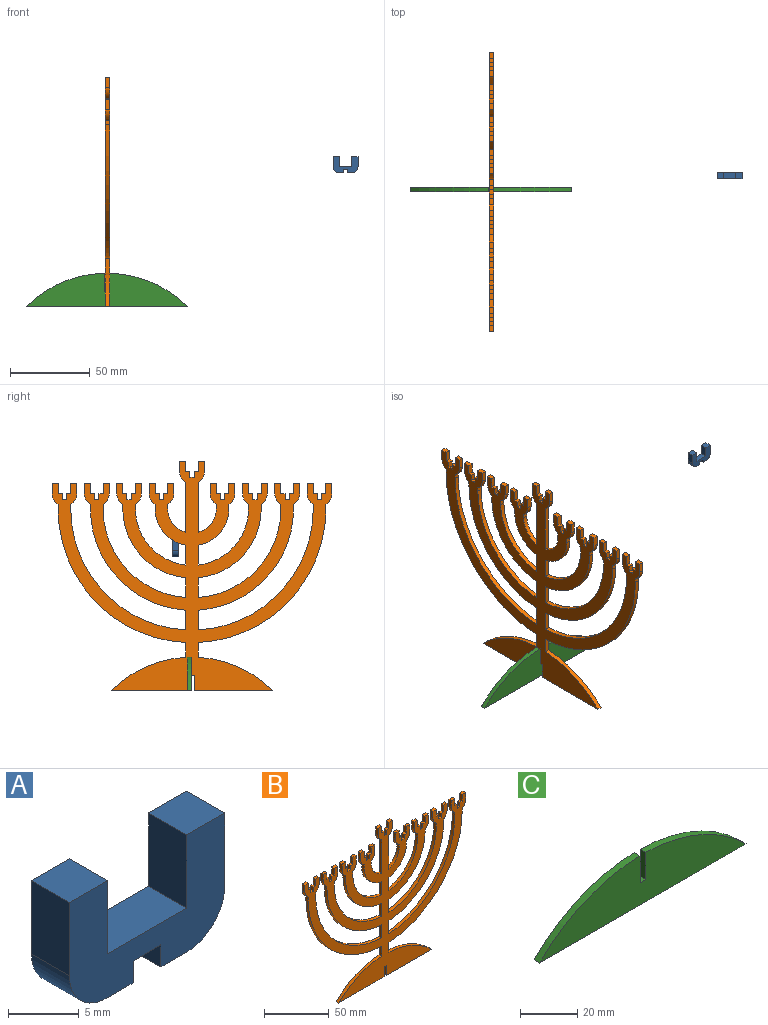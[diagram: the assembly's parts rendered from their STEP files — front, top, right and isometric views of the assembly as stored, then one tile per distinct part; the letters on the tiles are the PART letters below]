
ASSEMBLY  parts=3 mates=3
PART A: 16 faces, bbox 15.6x3.8x10.2 mm
  f0: cylinder r=3.81mm len=3.81mm, axis (0,1,0), area 22.8mm2, adj f1,f13,f14,f15
  f1: plane 6.35x3.81mm, normal (1,0,0), area 24.2mm2, adj f0,f2,f14,f15
  f2: plane 3.81x3.81mm, normal (0,0,1), area 14.5mm2, adj f1,f3,f14,f15
  f3: plane 6.35x3.81mm, normal (-1,0,0), area 24.2mm2, adj f2,f4,f14,f15
  f4: plane 7.94x3.81mm, normal (0,0,1), area 30.2mm2, adj f3,f5,f14,f15
  f5: plane 6.35x3.81mm, normal (1,0,0), area 24.2mm2, adj f4,f6,f14,f15
  f6: plane 3.81x3.81mm, normal (0,0,1), area 14.5mm2, adj f5,f7,f14,f15
  f7: plane 6.35x3.81mm, normal (-1,0,0), area 24.2mm2, adj f6,f8,f14,f15
  f8: cylinder r=3.81mm len=3.81mm, axis (0,1,0), area 22.8mm2, adj f7,f9,f14,f15
  f9: plane 3.81x2.57mm, normal (0,0,-1), area 9.8mm2, adj f8,f10,f14,f15
  f10: plane 3.81x1.91mm, normal (1,0,0), area 7.3mm2, adj f9,f11,f14,f15
  f11: plane 3.81x2.79mm, normal (0,0,-1), area 10.6mm2, adj f10,f12,f14,f15
  f12: plane 3.81x1.91mm, normal (-1,0,0), area 7.3mm2, adj f11,f13,f14,f15
  f13: plane 3.81x2.57mm, normal (0,0,-1), area 9.8mm2, adj f0,f12,f14,f15
  f14: plane 15.56x10.16mm, normal (0,-1,0), area 96.1mm2, adj f0,f1,f2,f3,f4,f5,f6,f7
  f15: plane 15.56x10.16mm, normal (0,1,0), area 96.1mm2, adj f0,f1,f2,f3,f4,f5,f6,f7
PART B: 168 faces, bbox 175.9x2.8x144.1 mm
  f0: plane 49.4x2.79mm, normal (0,0,-1), area 138mm2, adj f1,f2,f7,f167
  f1: plane 175.9x144.15mm, normal (0,-1,0), area 8346.4mm2, adj f0,f3,f4,f5,f6,f7,f8,f9
  f2: plane 175.9x144.15mm, normal (0,1,0), area 8346.4mm2, adj f0,f3,f4,f5,f6,f7,f8,f9
  f3: cylinder r=84.14mm len=84.04mm, axis (0,1,0), area 358.2mm2, adj f1,f2,f4,f164
  f4: plane 9.32x2.79mm, normal (-1,0,0), area 26.1mm2, adj f1,f2,f3,f5
  f5: cylinder r=71.84mm len=46.83mm, axis (0,1,0), area 146.6mm2, adj f1,f2,f4,f6
  f6: plane 49.4x2.79mm, normal (0,0,-1), area 138mm2, adj f1,f2,f5,f166
  f7: cylinder r=71.84mm len=46.83mm, axis (0,1,0), area 146.6mm2, adj f0,f1,f2,f8
  f8: plane 9.32x2.79mm, normal (1,0,0), area 26.1mm2, adj f1,f2,f7,f9
  f9: cylinder r=84.14mm len=84.04mm, axis (0,1,0), area 358.2mm2, adj f1,f2,f8,f10
  f10: plane 2.84x2.79mm, normal (1,0,0), area 7.9mm2, adj f1,f2,f9,f11
  f11: cylinder r=7.78mm len=6.69mm, axis (0,1,0), area 22.5mm2, adj f1,f2,f10,f12
  f12: plane 6.35x2.79mm, normal (1,0,0), area 17.7mm2, adj f1,f2,f11,f13
  f13: plane 3.81x2.79mm, normal (0,0,1), area 10.6mm2, adj f1,f2,f12,f14
  f14: plane 6.35x2.79mm, normal (-1,0,0), area 17.7mm2, adj f1,f2,f13,f15
  f15: plane 2.79x2.57mm, normal (0,0,1), area 7.2mm2, adj f1,f2,f14,f16
  f16: plane 3.81x2.79mm, normal (-1,0,0), area 10.6mm2, adj f1,f2,f15,f17
  f17: plane 2.79x2.79mm, normal (0,0,1), area 7.8mm2, adj f1,f2,f16,f18
  f18: plane 3.81x2.79mm, normal (1,0,0), area 10.6mm2, adj f1,f2,f17,f19
  f19: plane 2.79x2.57mm, normal (0,0,1), area 7.2mm2, adj f1,f2,f18,f20
  f20: plane 6.35x2.79mm, normal (1,0,0), area 17.7mm2, adj f1,f2,f19,f21
  f21: plane 3.81x2.79mm, normal (0,0,1), area 10.6mm2, adj f1,f2,f20,f22
  f22: plane 6.35x2.79mm, normal (-1,0,0), area 17.7mm2, adj f1,f2,f21,f23
  f23: cylinder r=7.78mm len=6.69mm, axis (0,1,0), area 22.5mm2, adj f1,f2,f22,f24
  f24: plane 2.84x2.79mm, normal (-1,0,0), area 7.9mm2, adj f1,f2,f23,f25
  f25: cylinder r=76.2mm len=76.1mm, axis (0,1,0), area 323.3mm2, adj f1,f2,f24,f26
  f26: plane 12.4x2.79mm, normal (1,0,0), area 34.7mm2, adj f1,f2,f25,f27
  f27: cylinder r=63.82mm len=63.69mm, axis (0,1,0), area 269mm2, adj f1,f2,f26,f28
  f28: plane 2.84x2.79mm, normal (1,0,0), area 7.9mm2, adj f1,f2,f27,f29
  f29: cylinder r=7.78mm len=6.69mm, axis (0,1,0), area 22.5mm2, adj f1,f2,f28,f30
  f30: plane 6.35x2.79mm, normal (1,0,0), area 17.7mm2, adj f1,f2,f29,f31
  f31: plane 3.81x2.79mm, normal (0,0,1), area 10.6mm2, adj f1,f2,f30,f32
  f32: plane 6.35x2.79mm, normal (-1,0,0), area 17.7mm2, adj f1,f2,f31,f33
  f33: plane 2.79x2.57mm, normal (0,0,1), area 7.2mm2, adj f1,f2,f32,f34
  f34: plane 3.81x2.79mm, normal (-1,0,0), area 10.6mm2, adj f1,f2,f33,f35
  f35: plane 2.79x2.79mm, normal (0,0,1), area 7.8mm2, adj f1,f2,f34,f36
  f36: plane 3.81x2.79mm, normal (1,0,0), area 10.6mm2, adj f1,f2,f35,f37
  f37: plane 2.79x2.57mm, normal (0,0,1), area 7.2mm2, adj f1,f2,f36,f38
  f38: plane 6.35x2.79mm, normal (1,0,0), area 17.7mm2, adj f1,f2,f37,f39
  f39: plane 3.81x2.79mm, normal (0,0,1), area 10.6mm2, adj f1,f2,f38,f40
  f40: plane 6.35x2.79mm, normal (-1,0,0), area 17.7mm2, adj f1,f2,f39,f41
  f41: cylinder r=7.78mm len=6.69mm, axis (0,1,0), area 22.5mm2, adj f1,f2,f40,f42
  f42: plane 2.84x2.79mm, normal (-1,0,0), area 7.9mm2, adj f1,f2,f41,f43
  f43: cylinder r=55.88mm len=55.74mm, axis (0,1,0), area 234.1mm2, adj f1,f2,f42,f44
  f44: plane 12.42x2.79mm, normal (1,0,0), area 34.7mm2, adj f1,f2,f43,f45
  f45: cylinder r=43.5mm len=43.32mm, axis (0,1,0), area 179.8mm2, adj f1,f2,f44,f46
  f46: plane 2.84x2.79mm, normal (1,0,0), area 7.9mm2, adj f1,f2,f45,f47
  f47: cylinder r=7.78mm len=6.69mm, axis (0,1,0), area 22.5mm2, adj f1,f2,f46,f48
  f48: plane 6.35x2.79mm, normal (1,0,0), area 17.7mm2, adj f1,f2,f47,f49
  f49: plane 3.81x2.79mm, normal (0,0,1), area 10.6mm2, adj f1,f2,f48,f50
  f50: plane 6.35x2.79mm, normal (-1,0,0), area 17.7mm2, adj f1,f2,f49,f51
  f51: plane 2.79x2.57mm, normal (0,0,1), area 7.2mm2, adj f1,f2,f50,f52
  f52: plane 3.81x2.79mm, normal (-1,0,0), area 10.6mm2, adj f1,f2,f51,f53
  f53: plane 2.79x2.79mm, normal (0,0,1), area 7.8mm2, adj f1,f2,f52,f54
  f54: plane 3.81x2.79mm, normal (1,0,0), area 10.6mm2, adj f1,f2,f53,f55
  f55: plane 2.79x2.57mm, normal (0,0,1), area 7.2mm2, adj f1,f2,f54,f56
  f56: plane 6.35x2.79mm, normal (1,0,0), area 17.7mm2, adj f1,f2,f55,f57
  f57: plane 3.81x2.79mm, normal (0,0,1), area 10.6mm2, adj f1,f2,f56,f58
  f58: plane 6.35x2.79mm, normal (-1,0,0), area 17.7mm2, adj f1,f2,f57,f59
  f59: cylinder r=7.78mm len=6.69mm, axis (0,1,0), area 22.5mm2, adj f1,f2,f58,f60
  f60: plane 2.84x2.79mm, normal (-1,0,0), area 7.9mm2, adj f1,f2,f59,f61
  f61: cylinder r=35.56mm len=35.34mm, axis (0,1,0), area 145mm2, adj f1,f2,f60,f62
  f62: plane 12.5x2.79mm, normal (1,0,0), area 34.9mm2, adj f1,f2,f61,f63
  f63: cylinder r=23.18mm len=22.84mm, axis (0,1,0), area 90.6mm2, adj f1,f2,f62,f64
  f64: plane 2.84x2.79mm, normal (1,0,0), area 7.9mm2, adj f1,f2,f63,f65
  f65: cylinder r=7.78mm len=6.69mm, axis (0,1,0), area 22.5mm2, adj f1,f2,f64,f66
  f66: plane 6.35x2.79mm, normal (1,0,0), area 17.7mm2, adj f1,f2,f65,f67
  f67: plane 3.81x2.79mm, normal (0,0,1), area 10.6mm2, adj f1,f2,f66,f68
  f68: plane 6.35x2.79mm, normal (-1,0,0), area 17.7mm2, adj f1,f2,f67,f69
  f69: plane 2.79x2.57mm, normal (0,0,1), area 7.2mm2, adj f1,f2,f68,f70
  f70: plane 3.81x2.79mm, normal (-1,0,0), area 10.6mm2, adj f1,f2,f69,f71
  f71: plane 2.79x2.79mm, normal (0,0,1), area 7.8mm2, adj f1,f2,f70,f72
  f72: plane 3.81x2.79mm, normal (1,0,0), area 10.6mm2, adj f1,f2,f71,f73
  f73: plane 2.79x2.57mm, normal (0,0,1), area 7.2mm2, adj f1,f2,f72,f74
  f74: plane 6.35x2.79mm, normal (1,0,0), area 17.7mm2, adj f1,f2,f73,f75
  f75: plane 3.81x2.79mm, normal (0,0,1), area 10.6mm2, adj f1,f2,f74,f76
  f76: plane 6.35x2.79mm, normal (-1,0,0), area 17.7mm2, adj f1,f2,f75,f77
  f77: cylinder r=7.78mm len=6.69mm, axis (0,1,0), area 22.5mm2, adj f1,f2,f76,f78
  f78: plane 2.84x2.79mm, normal (-1,0,0), area 7.9mm2, adj f1,f2,f77,f79
  f79: cylinder r=15.24mm len=14.71mm, axis (0,1,0), area 55.7mm2, adj f1,f2,f78,f80
  f80: plane 31.52x2.79mm, normal (1,0,0), area 88.1mm2, adj f1,f2,f79,f81
  f81: cylinder r=7.78mm len=6.69mm, axis (0,1,0), area 22.5mm2, adj f1,f2,f80,f82
  f82: plane 6.35x2.79mm, normal (1,0,0), area 17.7mm2, adj f1,f2,f81,f83
  f83: plane 3.81x2.79mm, normal (0,0,1), area 10.6mm2, adj f1,f2,f82,f84
  f84: plane 6.35x2.79mm, normal (-1,0,0), area 17.7mm2, adj f1,f2,f83,f85
  f85: plane 2.79x2.57mm, normal (0,0,1), area 7.2mm2, adj f1,f2,f84,f86
  f86: plane 3.81x2.79mm, normal (-1,0,0), area 10.6mm2, adj f1,f2,f85,f87
  f87: plane 2.79x2.79mm, normal (0,0,1), area 7.8mm2, adj f1,f2,f86,f88
  f88: plane 3.81x2.79mm, normal (1,0,0), area 10.6mm2, adj f1,f2,f87,f89
  f89: plane 2.79x2.57mm, normal (0,0,1), area 7.2mm2, adj f1,f2,f88,f90
  f90: plane 6.35x2.79mm, normal (1,0,0), area 17.7mm2, adj f1,f2,f89,f91
  f91: plane 3.81x2.79mm, normal (0,0,1), area 10.6mm2, adj f1,f2,f90,f92
  f92: plane 6.35x2.79mm, normal (-1,0,0), area 17.7mm2, adj f1,f2,f91,f93
  f93: cylinder r=7.78mm len=6.69mm, axis (0,1,0), area 22.5mm2, adj f1,f2,f92,f94
  f94: plane 31.52x2.79mm, normal (-1,0,0), area 88.1mm2, adj f1,f2,f93,f95
  f95: cylinder r=15.24mm len=14.71mm, axis (0,1,0), area 55.7mm2, adj f1,f2,f94,f96
  f96: plane 2.84x2.79mm, normal (1,0,0), area 7.9mm2, adj f1,f2,f95,f97
  f97: cylinder r=7.78mm len=6.69mm, axis (0,1,0), area 22.5mm2, adj f1,f2,f96,f98
  f98: plane 6.35x2.79mm, normal (1,0,0), area 17.7mm2, adj f1,f2,f97,f99
  f99: plane 3.81x2.79mm, normal (0,0,1), area 10.6mm2, adj f1,f2,f98,f100
  f100: plane 6.35x2.79mm, normal (-1,0,0), area 17.7mm2, adj f1,f2,f99,f101
  f101: plane 2.79x2.57mm, normal (0,0,1), area 7.2mm2, adj f1,f2,f100,f102
  f102: plane 3.81x2.79mm, normal (-1,0,0), area 10.6mm2, adj f1,f2,f101,f103
  f103: plane 2.79x2.79mm, normal (0,0,1), area 7.8mm2, adj f1,f2,f102,f104
  f104: plane 3.81x2.79mm, normal (1,0,0), area 10.6mm2, adj f1,f2,f103,f105
  f105: plane 2.79x2.57mm, normal (0,0,1), area 7.2mm2, adj f1,f2,f104,f106
  f106: plane 6.35x2.79mm, normal (1,0,0), area 17.7mm2, adj f1,f2,f105,f107
  f107: plane 3.81x2.79mm, normal (0,0,1), area 10.6mm2, adj f1,f2,f106,f108
  f108: plane 6.35x2.79mm, normal (-1,0,0), area 17.7mm2, adj f1,f2,f107,f109
  f109: cylinder r=7.78mm len=6.69mm, axis (0,1,0), area 22.5mm2, adj f1,f2,f108,f110
  f110: plane 2.84x2.79mm, normal (-1,0,0), area 7.9mm2, adj f1,f2,f109,f111
  f111: cylinder r=23.18mm len=22.84mm, axis (0,1,0), area 90.6mm2, adj f1,f2,f110,f112
  f112: plane 12.5x2.79mm, normal (-1,0,0), area 34.9mm2, adj f1,f2,f111,f113
  f113: cylinder r=35.56mm len=35.34mm, axis (0,1,0), area 145mm2, adj f1,f2,f112,f114
  f114: plane 2.84x2.79mm, normal (1,0,0), area 7.9mm2, adj f1,f2,f113,f115
  f115: cylinder r=7.78mm len=6.69mm, axis (0,1,0), area 22.5mm2, adj f1,f2,f114,f116
  f116: plane 6.35x2.79mm, normal (1,0,0), area 17.7mm2, adj f1,f2,f115,f117
  f117: plane 3.81x2.79mm, normal (0,0,1), area 10.6mm2, adj f1,f2,f116,f118
  f118: plane 6.35x2.79mm, normal (-1,0,0), area 17.7mm2, adj f1,f2,f117,f119
  f119: plane 2.79x2.57mm, normal (0,0,1), area 7.2mm2, adj f1,f2,f118,f120
  f120: plane 3.81x2.79mm, normal (-1,0,0), area 10.6mm2, adj f1,f2,f119,f121
  f121: plane 2.79x2.79mm, normal (0,0,1), area 7.8mm2, adj f1,f2,f120,f122
  f122: plane 3.81x2.79mm, normal (1,0,0), area 10.6mm2, adj f1,f2,f121,f123
  f123: plane 2.79x2.57mm, normal (0,0,1), area 7.2mm2, adj f1,f2,f122,f124
  f124: plane 6.35x2.79mm, normal (1,0,0), area 17.7mm2, adj f1,f2,f123,f125
  f125: plane 3.81x2.79mm, normal (0,0,1), area 10.6mm2, adj f1,f2,f124,f126
  f126: plane 6.35x2.79mm, normal (-1,0,0), area 17.7mm2, adj f1,f2,f125,f127
  f127: cylinder r=7.78mm len=6.69mm, axis (0,1,0), area 22.5mm2, adj f1,f2,f126,f128
  f128: plane 2.84x2.79mm, normal (-1,0,0), area 7.9mm2, adj f1,f2,f127,f129
  f129: cylinder r=43.5mm len=43.32mm, axis (0,1,0), area 179.8mm2, adj f1,f2,f128,f130
  f130: plane 12.42x2.79mm, normal (-1,0,0), area 34.7mm2, adj f1,f2,f129,f131
  f131: cylinder r=55.88mm len=55.74mm, axis (0,1,0), area 234.1mm2, adj f1,f2,f130,f132
  f132: plane 2.84x2.79mm, normal (1,0,0), area 7.9mm2, adj f1,f2,f131,f133
  f133: cylinder r=7.78mm len=6.69mm, axis (0,1,0), area 22.5mm2, adj f1,f2,f132,f134
  f134: plane 6.35x2.79mm, normal (1,0,0), area 17.7mm2, adj f1,f2,f133,f135
  f135: plane 3.81x2.79mm, normal (0,0,1), area 10.6mm2, adj f1,f2,f134,f136
  f136: plane 6.35x2.79mm, normal (-1,0,0), area 17.7mm2, adj f1,f2,f135,f137
  f137: plane 2.79x2.57mm, normal (0,0,1), area 7.2mm2, adj f1,f2,f136,f138
  f138: plane 3.81x2.79mm, normal (-1,0,0), area 10.6mm2, adj f1,f2,f137,f139
  f139: plane 2.79x2.79mm, normal (0,0,1), area 7.8mm2, adj f1,f2,f138,f140
  f140: plane 3.81x2.79mm, normal (1,0,0), area 10.6mm2, adj f1,f2,f139,f141
  f141: plane 2.79x2.57mm, normal (0,0,1), area 7.2mm2, adj f1,f2,f140,f142
  f142: plane 6.35x2.79mm, normal (1,0,0), area 17.7mm2, adj f1,f2,f141,f143
  f143: plane 3.81x2.79mm, normal (0,0,1), area 10.6mm2, adj f1,f2,f142,f144
  f144: plane 6.35x2.79mm, normal (-1,0,0), area 17.7mm2, adj f1,f2,f143,f145
  f145: cylinder r=7.78mm len=6.69mm, axis (0,1,0), area 22.5mm2, adj f1,f2,f144,f146
  f146: plane 2.84x2.79mm, normal (-1,0,0), area 7.9mm2, adj f1,f2,f145,f147
  f147: cylinder r=63.82mm len=63.69mm, axis (0,1,0), area 269mm2, adj f1,f2,f146,f148
  f148: plane 12.4x2.79mm, normal (-1,0,0), area 34.7mm2, adj f1,f2,f147,f149
  f149: cylinder r=76.2mm len=76.1mm, axis (0,1,0), area 323.3mm2, adj f1,f2,f148,f150
  f150: plane 2.84x2.79mm, normal (1,0,0), area 7.9mm2, adj f1,f2,f149,f151
  f151: cylinder r=7.78mm len=6.69mm, axis (0,1,0), area 22.5mm2, adj f1,f2,f150,f152
  f152: plane 6.35x2.79mm, normal (1,0,0), area 17.7mm2, adj f1,f2,f151,f153
  f153: plane 3.81x2.79mm, normal (0,0,1), area 10.6mm2, adj f1,f2,f152,f154
  f154: plane 6.35x2.79mm, normal (-1,0,0), area 17.7mm2, adj f1,f2,f153,f155
  f155: plane 2.79x2.57mm, normal (0,0,1), area 7.2mm2, adj f1,f2,f154,f156
  f156: plane 3.81x2.79mm, normal (-1,0,0), area 10.6mm2, adj f1,f2,f155,f157
  f157: plane 2.79x2.79mm, normal (0,0,1), area 7.8mm2, adj f1,f2,f156,f158
  f158: plane 3.81x2.79mm, normal (1,0,0), area 10.6mm2, adj f1,f2,f157,f159
  f159: plane 2.79x2.57mm, normal (0,0,1), area 7.2mm2, adj f1,f2,f158,f160
  f160: plane 6.35x2.79mm, normal (1,0,0), area 17.7mm2, adj f1,f2,f159,f161
  f161: plane 3.81x2.79mm, normal (0,0,1), area 10.6mm2, adj f1,f2,f160,f162
  f162: plane 6.35x2.79mm, normal (-1,0,0), area 17.7mm2, adj f1,f2,f161,f163
  f163: cylinder r=7.78mm len=6.69mm, axis (0,1,0), area 22.5mm2, adj f1,f2,f162,f164
  f164: plane 2.84x2.79mm, normal (-1,0,0), area 7.9mm2, adj f1,f2,f3,f163
  f165: plane 2.79x2.79mm, normal (0,0,-1), area 7.8mm2, adj f1,f2,f166,f167
  f166: plane 9.53x2.79mm, normal (1,0,0), area 26.6mm2, adj f1,f2,f6,f165
  f167: plane 9.53x2.79mm, normal (-1,0,0), area 26.6mm2, adj f0,f1,f2,f165
PART C: 8 faces, bbox 101.6x2.8x21 mm
  f0: plane 11.5x2.79mm, normal (1,0,0), area 32.1mm2, adj f1,f5,f6,f7
  f1: cylinder r=71.84mm len=49.4mm, axis (0,1,0), area 153.7mm2, adj f0,f2,f6,f7
  f2: plane 101.6x2.79mm, normal (0,0,-1), area 283.9mm2, adj f1,f3,f6,f7
  f3: cylinder r=71.84mm len=49.4mm, axis (0,1,0), area 153.7mm2, adj f2,f4,f6,f7
  f4: plane 11.5x2.79mm, normal (-1,0,0), area 32.1mm2, adj f3,f5,f6,f7
  f5: plane 2.79x2.79mm, normal (0,0,1), area 7.8mm2, adj f0,f4,f6,f7
  f6: plane 101.6x21.03mm, normal (0,-1,0), area 1440.9mm2, adj f0,f1,f2,f3,f4,f5
  f7: plane 101.6x21.03mm, normal (0,1,0), area 1440.9mm2, adj f0,f1,f2,f3,f4,f5
PLACE A t=(-12.93,-9.79,133.44)mm
PLACE B rot(axis=(0,0,1),90deg) t=(-164.07,-21.93,45.57)mm
PLACE C t=(-162.98,-18.79,45.53)mm
MATE parallel B.f0 <-> C.f2  axis (0,0,-1) through (-162.67,4.17,45.57)mm
MATE parallel A.f2 <-> B.f83  axis (0,0,1) through (-7.06,-11.69,139.79)mm
MATE parallel A.f10 <-> B.f1  axis (1,0,0) through (-14.33,-11.69,130.58)mm
